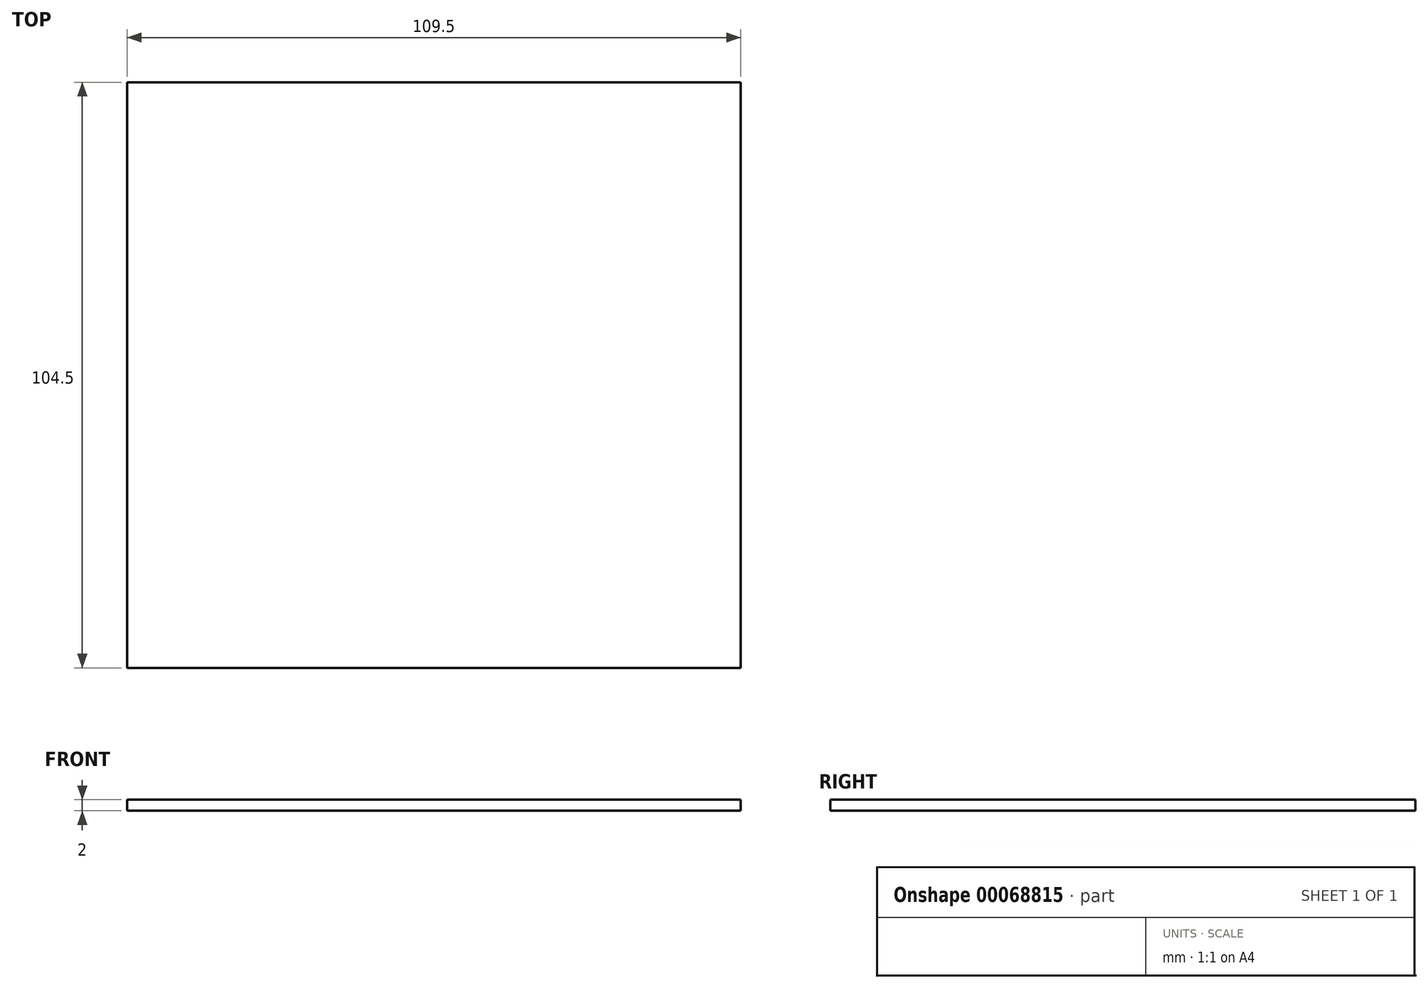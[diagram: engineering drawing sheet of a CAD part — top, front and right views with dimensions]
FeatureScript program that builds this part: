
annotation { "Feature Type Name" : "Feature", "Feature Type Description" : "" }
export const myFeature = defineFeature(function(context is Context, id is Id, definition is map)
    precondition{}
    {
        {
            var Q0;
            Q0=qCreatedBy(makeId("Top.planeOp"),FACE);
            var sketch = newSketch(context, id + "F0", { "sketchPlane" : qUnion([Q0])});
            skLineSegment(sketch, "E0.bottom", {"start": v(0, 0) * mm, "end": v(109.5, 0) * mm});
            skLineSegment(sketch, "E0.top", {"start": v(0, -104.5) * mm, "end": v(109.5, -104.5) * mm});
            skLineSegment(sketch, "E0.left", {"start": v(0, 0) * mm, "end": v(0, -104.5) * mm});
            skLineSegment(sketch, "E0.right", {"start": v(109.5, 0) * mm, "end": v(109.5, -104.5) * mm});
            skSolve(sketch);
        }
        {
            var Q0;
            Q0 = qSketchRegion(id + "F0", true);
            extrude(context, id + "F1", {"entities" : qUnion([Q0]), "depth" : 2 * mm});
        }
    });
